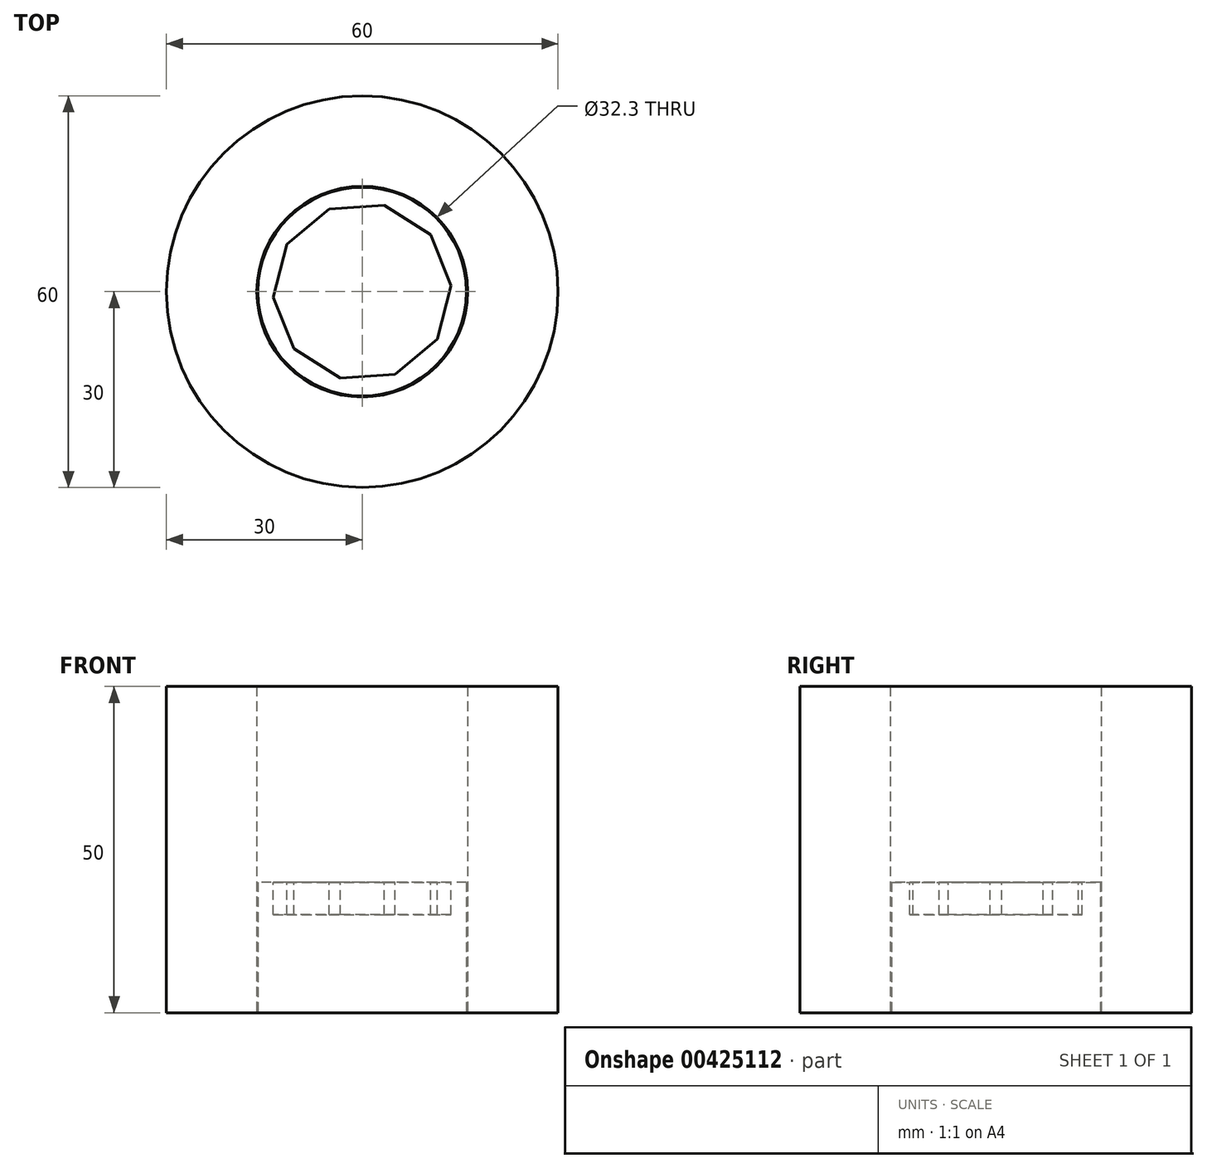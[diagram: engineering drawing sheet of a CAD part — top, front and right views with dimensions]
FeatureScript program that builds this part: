
annotation { "Feature Type Name" : "Feature", "Feature Type Description" : "" }
export const myFeature = defineFeature(function(context is Context, id is Id, definition is map)
    precondition{}
    {
        {
            var Q0;
            Q0=qCreatedBy(makeId("Top.planeOp"),FACE);
            var sketch = newSketch(context, id + "F0", { "sketchPlane" : qUnion([Q0])});
            skCircle(sketch, "E0", {"center": v(0, 0) * mm, "radius": 16.15 * mm});
            skCircle(sketch, "E1", {"center": v(0, 0) * mm, "radius": 30 * mm});
            skSolve(sketch);
        }
        {
            var Q0;
            Q0 = qSketchRegion(id + "F0", true);
            extrude(context, id + "F1", {"entities" : qUnion([Q0]), "depth" : 50 * mm});
        }
        {
            var Q0;
            Q0=qCreatedBy(makeId("Top.planeOp"),FACE);
            var sketch = newSketch(context, id + "F2", { "sketchPlane" : qUnion([Q0])});
            skCircle(sketch, "E2", {"center": v(0, 0) * mm, "radius": 15.98 * mm});
            skSolve(sketch);
        }
        {
            var Q0;
            Q0 = qSketchRegion(id + "F2", true);
            extrude(context, id + "F3", {"entities" : qUnion([Q0]), "depth" : 20 * mm});
        }
        {
            var Q0;
            Q0=makeQuery(id+"F3.opExtrude","CAP_FACE",FACE,{"disambiguationData":[OSD([sQuery(id+"F2.wireOp",EDGE,"E2")])],"isStart":false});
            var sketch = newSketch(context, id + "F4", { "sketchPlane" : qUnion([Q0])});
            skSolve(sketch);
        }
        {
            var Q0;
            Q0=makeQuery(id+"F4.imprint","IMPRINT",FACE,{"disambiguationData":[TD([[makeQuery(id+"F4.imprint","IMPRINT",EDGE,{"derivedFrom":makeQuery(id+"F3.opExtrude","CAP_EDGE",EDGE,{"disambiguationData":[OSD([sQuery(id+"F2.wireOp",EDGE,"E2")])],"isStart":false})}),1.0]])]});
            var sketch = newSketch(context, id + "F5", { "sketchPlane" : qUnion([Q0])});
            skCircle(sketch, "E3.cCircle", {"center": v(0, 0) * mm, "radius": 12.97 * mm, "construction": true});
            skLineSegment(sketch, "E3.0", {"start": v(-11.53, 7.28) * mm, "end": v(-5.05, 12.67) * mm});
            skLineSegment(sketch, "E3.1", {"start": v(-5.05, 12.67) * mm, "end": v(3.36, 13.22) * mm});
            skLineSegment(sketch, "E3.2", {"start": v(3.36, 13.22) * mm, "end": v(10.49, 8.72) * mm});
            skLineSegment(sketch, "E3.3", {"start": v(10.49, 8.72) * mm, "end": v(13.6, 0.9) * mm});
            skLineSegment(sketch, "E3.4", {"start": v(13.6, 0.9) * mm, "end": v(11.53, -7.28) * mm});
            skLineSegment(sketch, "E3.5", {"start": v(11.53, -7.28) * mm, "end": v(5.05, -12.67) * mm});
            skLineSegment(sketch, "E3.6", {"start": v(5.05, -12.67) * mm, "end": v(-3.36, -13.22) * mm});
            skLineSegment(sketch, "E3.7", {"start": v(-3.36, -13.22) * mm, "end": v(-10.49, -8.72) * mm});
            skLineSegment(sketch, "E3.8", {"start": v(-10.49, -8.72) * mm, "end": v(-13.6, -0.9) * mm});
            skLineSegment(sketch, "E3.9", {"start": v(-13.6, -0.9) * mm, "end": v(-11.53, 7.28) * mm});
            skPoint(sketch, "E3.0.midPoint", {"position": v(-8.3, 9.97) * mm});
            skSolve(sketch);
        }
        {
            var Q0;
            Q0 = qSketchRegion(id + "F5", true);
            extrude(context, id + "F6", {"entities" : qUnion([Q0]), "operationType" : NewBodyOperationType.REMOVE, "oppositeDirection" : true, "depth" : 5 * mm});
        }
        {
            var Q0;
            Q0=makeQuery(id+"F4.imprint","IMPRINT",FACE,{"disambiguationData":[TD([[makeQuery(id+"F4.imprint","IMPRINT",EDGE,{"derivedFrom":makeQuery(id+"F3.opExtrude","CAP_EDGE",EDGE,{"disambiguationData":[OSD([sQuery(id+"F2.wireOp",EDGE,"E2")])],"isStart":false})}),1.0]])]});
            var sketch = newSketch(context, id + "F7", { "sketchPlane" : qUnion([Q0])});
            skCircle(sketch, "E4", {"center": v(0, 0) * mm, "radius": 5 * mm});
            skSolve(sketch);
        }
        {
            var Q0;
            Q0 = qSketchRegion(id + "F7", true);
            extrude(context, id + "F8", {"entities" : qUnion([Q0]), "operationType" : NewBodyOperationType.REMOVE, "oppositeDirection" : true, "depth" : 5 * mm});
        }
        {
            var Q0;
            Q0 = qSketchRegion(id + "F7", true);
            extrude(context, id + "F9", {"entities" : qUnion([Q0]), "operationType" : NewBodyOperationType.REMOVE, "oppositeDirection" : true, "depth" : 5 * mm});
        }
    });
